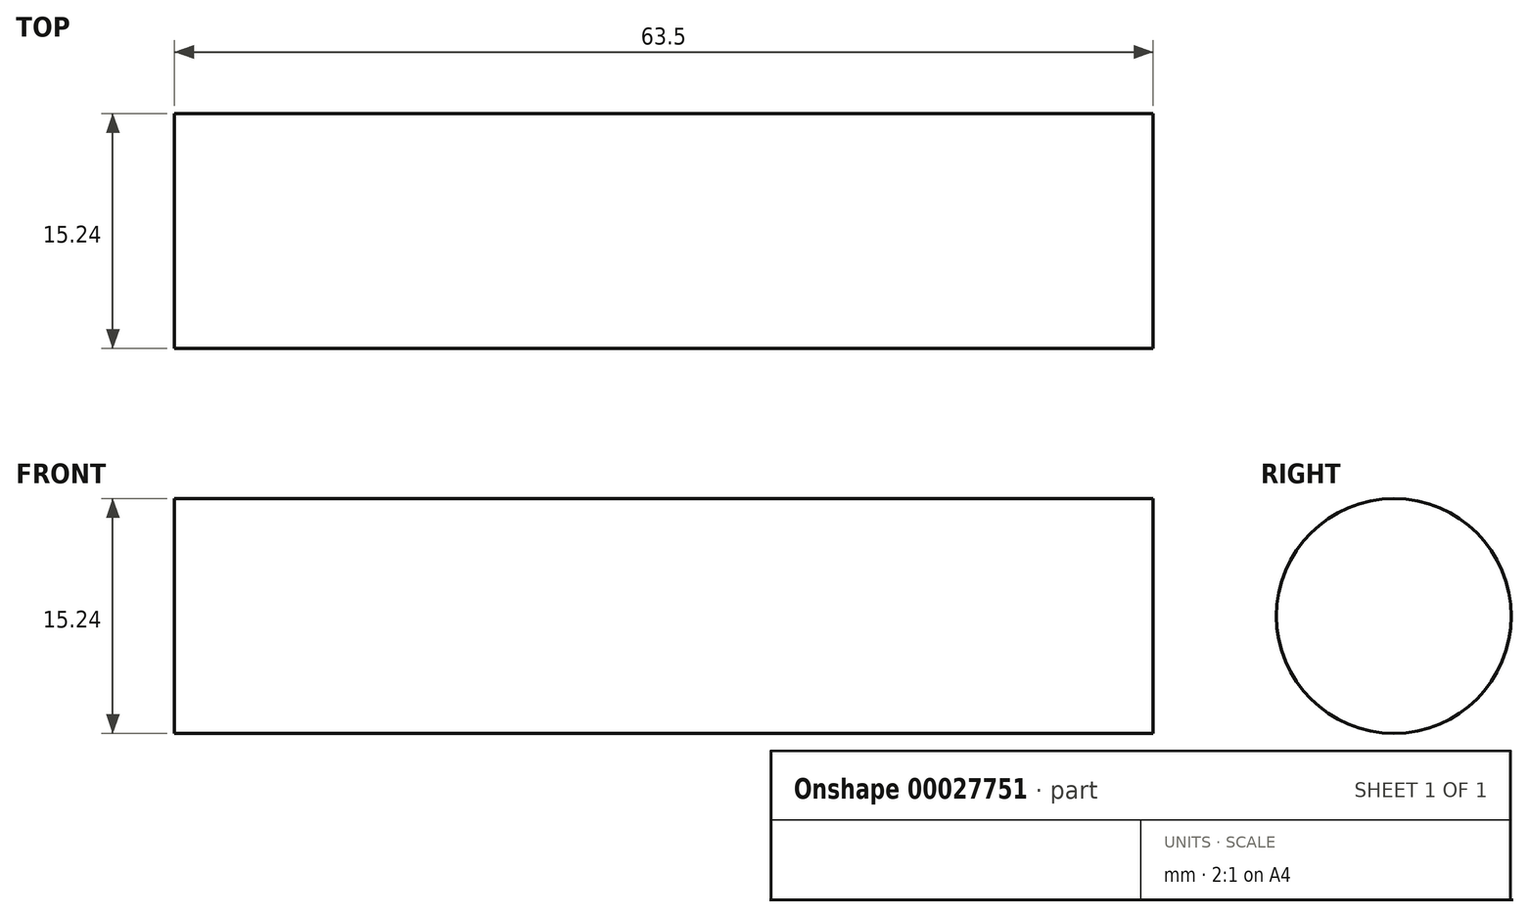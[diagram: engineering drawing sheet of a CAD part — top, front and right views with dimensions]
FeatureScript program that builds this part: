
annotation { "Feature Type Name" : "Feature", "Feature Type Description" : "" }
export const myFeature = defineFeature(function(context is Context, id is Id, definition is map)
    precondition{}
    {
        {
            var Q0;
            Q0=qCreatedBy(makeId("Right.planeOp"),FACE);
            var sketch = newSketch(context, id + "F0", { "sketchPlane" : qUnion([Q0])});
            skCircle(sketch, "E0", {"center": v(0, 0) * mm, "radius": 7.62 * mm});
            skSolve(sketch);
        }
        {
            var Q0;
            Q0 = qSketchRegion(id + "F0", true);
            extrude(context, id + "F1", {"entities" : qUnion([Q0]), "endBound" : BoundingType.SYMMETRIC, "depth" : 63.5 * mm});
        }
    });
